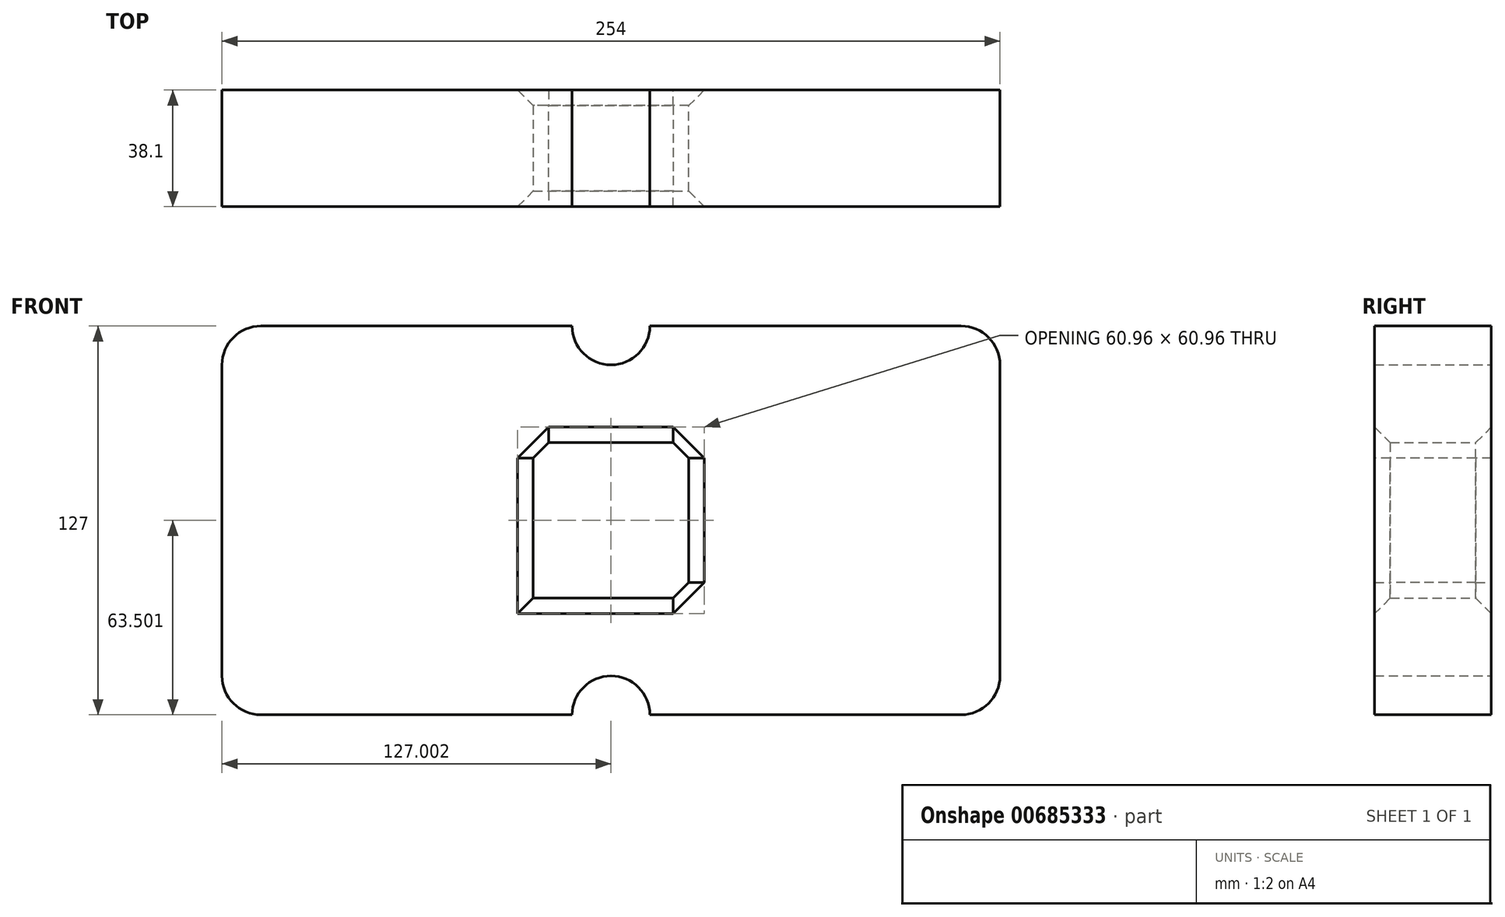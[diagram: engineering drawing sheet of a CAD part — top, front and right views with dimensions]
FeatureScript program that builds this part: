
annotation { "Feature Type Name" : "Feature", "Feature Type Description" : "" }
export const myFeature = defineFeature(function(context is Context, id is Id, definition is map)
    precondition{}
    {
        {
            var Q0;
            Q0=qCreatedBy(makeId("Front.planeOp"),FACE);
            var sketch = newSketch(context, id + "F0", { "sketchPlane" : qUnion([Q0])});
            skLineSegment(sketch, "E0.bottom", {"start": v(-116.43, 76.44) * mm, "end": v(-14.83, 76.44) * mm});
            skLineSegment(sketch, "E0.top", {"start": v(-116.43, -50.56) * mm, "end": v(-14.83, -50.56) * mm});
            skLineSegment(sketch, "E0.left", {"start": v(-129.13, 63.74) * mm, "end": v(-129.13, -37.86) * mm});
            skLineSegment(sketch, "E0.right", {"start": v(124.87, 63.74) * mm, "end": v(124.87, -37.86) * mm});
            skPoint(sketch, "E1.visualSharp", {"position": v(-129.13, 76.44) * mm});
            skArc(sketch, "E1.filletArc", {"start": v(-116.43, 76.44) * mm, "mid": v(-125.4, 72.72) * mm, "end": v(-129.13, 63.74) * mm});
            skPoint(sketch, "E2.visualSharp", {"position": v(124.87, -50.56) * mm});
            skArc(sketch, "E2.filletArc", {"start": v(112.17, -50.56) * mm, "mid": v(121.15, -46.84) * mm, "end": v(124.87, -37.86) * mm});
            skPoint(sketch, "E3.visualSharp", {"position": v(124.87, 76.44) * mm});
            skArc(sketch, "E3.filletArc", {"start": v(124.87, 63.74) * mm, "mid": v(121.15, 72.72) * mm, "end": v(112.17, 76.44) * mm});
            skPoint(sketch, "E4.visualSharp", {"position": v(-129.13, -50.56) * mm});
            skArc(sketch, "E4.filletArc", {"start": v(-129.13, -37.86) * mm, "mid": v(-125.4, -46.84) * mm, "end": v(-116.43, -50.56) * mm});
            skArc(sketch, "E5", {"start": v(-14.83, 76.44) * mm, "mid": v(-2.13, 63.74) * mm, "end": v(10.57, 76.44) * mm});
            skArc(sketch, "E6", {"start": v(10.57, -50.56) * mm, "mid": v(-2.13, -37.86) * mm, "end": v(-14.83, -50.56) * mm});
            skLineSegment(sketch, "E7.trimOffspring", {"start": v(10.57, 76.44) * mm, "end": v(112.17, 76.44) * mm});
            skLineSegment(sketch, "E8.trimOffspring", {"start": v(10.57, -50.56) * mm, "end": v(112.17, -50.56) * mm});
            skLineSegment(sketch, "E9", {"start": v(-27.53, 38.34) * mm, "end": v(-27.53, -12.46) * mm});
            skLineSegment(sketch, "E10", {"start": v(-27.53, -12.46) * mm, "end": v(23.27, -12.46) * mm});
            skLineSegment(sketch, "E11", {"start": v(23.27, -12.46) * mm, "end": v(23.27, 38.34) * mm});
            skLineSegment(sketch, "E12", {"start": v(-27.53, 38.34) * mm, "end": v(23.27, 38.34) * mm});
            skSolve(sketch);
        }
        {
            var Q0;
            Q0 = qSketchRegion(id + "F0", true);
            extrude(context, id + "F1", {"entities" : qUnion([Q0]), "depth" : 38.1 * mm, "offsetDistance" : 25.4 * mm});
        }
        {
            var Q0;
            Q0=makeQuery(id+"F1.opExtrude","SWEPT_FACE",FACE,{"disambiguationData":[OSD([sQuery(id+"F0.wireOp",EDGE,"E11")])]});
            var Q1;
            Q1=makeQuery(id+"F1.opExtrude","SWEPT_FACE",FACE,{"disambiguationData":[OSD([sQuery(id+"F0.wireOp",EDGE,"E12")])]});
            chamfer(context, id + "F2", {"entities" : qUnion([Q0, Q1]), "width" : 5.08 * mm, "tangentPropagation" : true});
        }
    });
